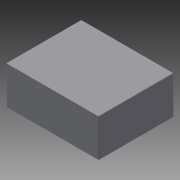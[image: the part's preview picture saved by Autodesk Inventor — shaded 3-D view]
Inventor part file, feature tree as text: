
AUTODESK INVENTOR PART (.ipt)
format: ipt  version: 2013 (Build 170138000, 138)  size: 88,064 bytes
history: native  units: in
note: dims shown in document units (in); Inventor stores cm internally (conversion verified against a paired STEP export)
features: reference x3, extrude x1, fillet x1, sketch x1
ambient origin geometry x8: Origin, YZ Plane, XZ Plane, XY Plane, X Axis, Y Axis, Z Axis, Center Point
bodies: Solid1 (feature_tree)
feature tree (6):
  extrude  "Extrusion1"  Depth=2.97in
  fillet  "Fillet1"  Radius=5.74in
  sketch  "Sketch1"  dims[d0=7.07in d1=2.97in d2=5.74in d3=0.0in d4=0.05in]
  reference  "Reference1"
  reference  "Reference2"
  reference  "Reference3"
